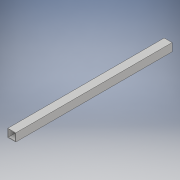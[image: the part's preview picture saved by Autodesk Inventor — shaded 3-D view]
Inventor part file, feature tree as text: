
AUTODESK INVENTOR PART (.ipt)
format: ipt  version: 2019.3 (Build 233278000, 278)  size: 102,912 bytes
history: native  units: mm
features: other x3, reference x2, extrude x1, sketch x1
ambient origin geometry x8: Origin, YZ Plane, XZ Plane, XY Plane, X Axis, Y Axis, Z Axis, Center Point
bodies: Solid1 (feature_tree)
feature tree (7):
  extrude  "Extrusion1"  Depth=22.225mm
  sketch  "Sketch1"  dims[d0=22.225mm d1=22.225mm d2=1.5875mm d3=1.5875mm d8=500.0mm d9=0.0mm]
  reference  "Reference1"
  reference  "Reference2"
  parser-record x1  (decoder bookkeeping rows leaked as tree rows — omitted from the tree; the rows remain in map.json)
  other  "Assembly.iam"
  other  "RailMount:1"
note: 1 file-system path scrubbed to <path> (originals preserved in map.json)
